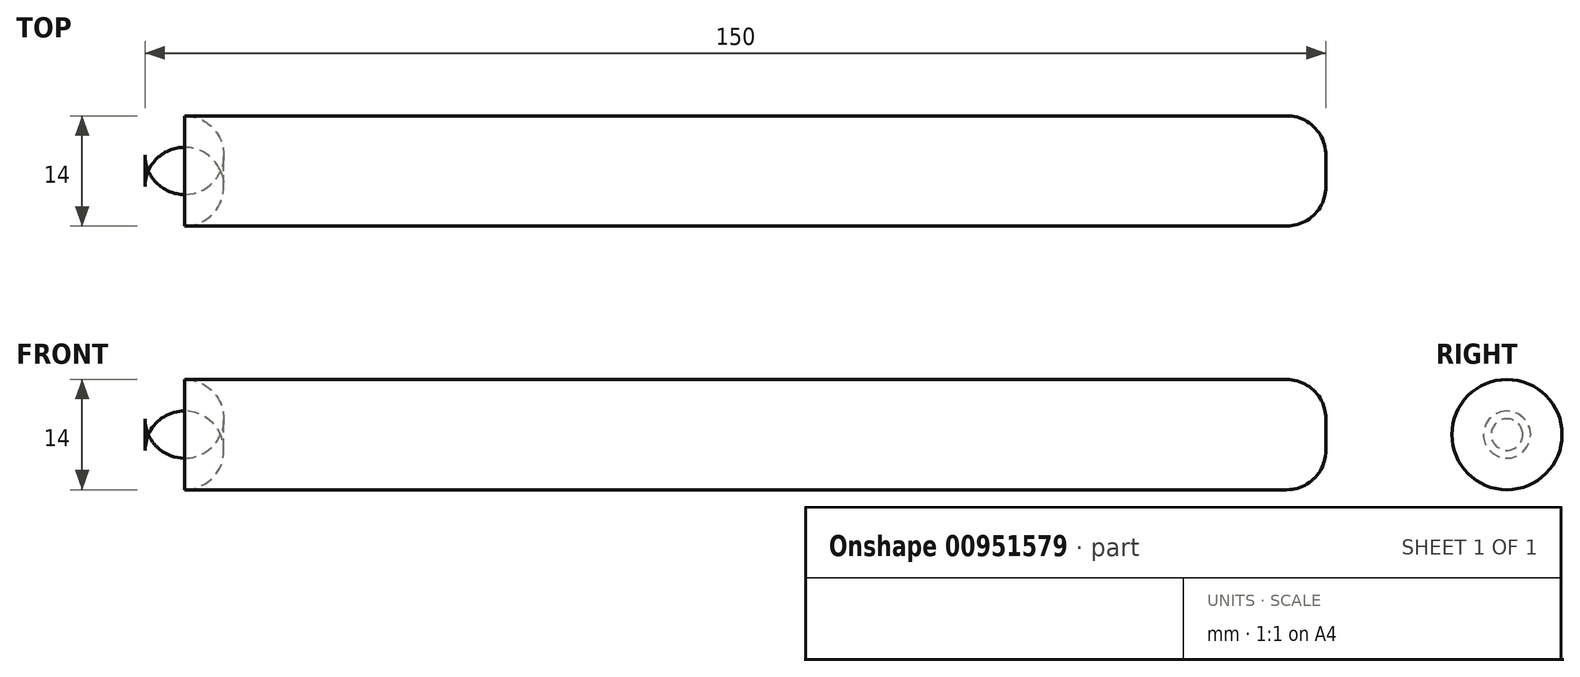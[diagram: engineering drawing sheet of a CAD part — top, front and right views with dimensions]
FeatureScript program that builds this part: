
annotation { "Feature Type Name" : "Feature", "Feature Type Description" : "" }
export const myFeature = defineFeature(function(context is Context, id is Id, definition is map)
    precondition{}
    {
        {
            var Q0;
            Q0=qCreatedBy(makeId("Right.planeOp"),FACE);
            var sketch = newSketch(context, id + "F0", { "sketchPlane" : qUnion([Q0])});
            skCircle(sketch, "E0", {"center": v(0, 0) * mm, "radius": 7 * mm});
            skSolve(sketch);
        }
        {
            var Q0;
            Q0=makeQuery(id+"F0.imprint","IMPRINT",FACE,{"disambiguationData":[TD([[makeQuery(id+"F0.imprint","IMPRINT",EDGE,{"derivedFrom":sQuery(id+"F0.wireOp",EDGE,"E0")}),1.0]])]});
            extrude(context, id + "F1", {"entities" : qUnion([Q0]), "endBound" : BoundingType.SYMMETRIC, "depth" : 150 * mm, "offsetDistance" : 25 * mm});
        }
        {
            var Q0;
            Q0=makeQuery(id+"F1.opExtrude","CAP_EDGE",EDGE,{"disambiguationData":[OSD([sQuery(id+"F0.wireOp",EDGE,"E0")])],"isStart":false});
            var Q1;
            Q1=makeQuery(id+"F1.opExtrude","CAP_EDGE",EDGE,{"disambiguationData":[OSD([sQuery(id+"F0.wireOp",EDGE,"E0")])],"isStart":true});
            fillet(context, id + "F2", {"entities" : qUnion([Q0, Q1]), "radius" : 5 * mm, "tangentPropagation" : true, "allowEdgeOverflow" : false});
        }
    });
